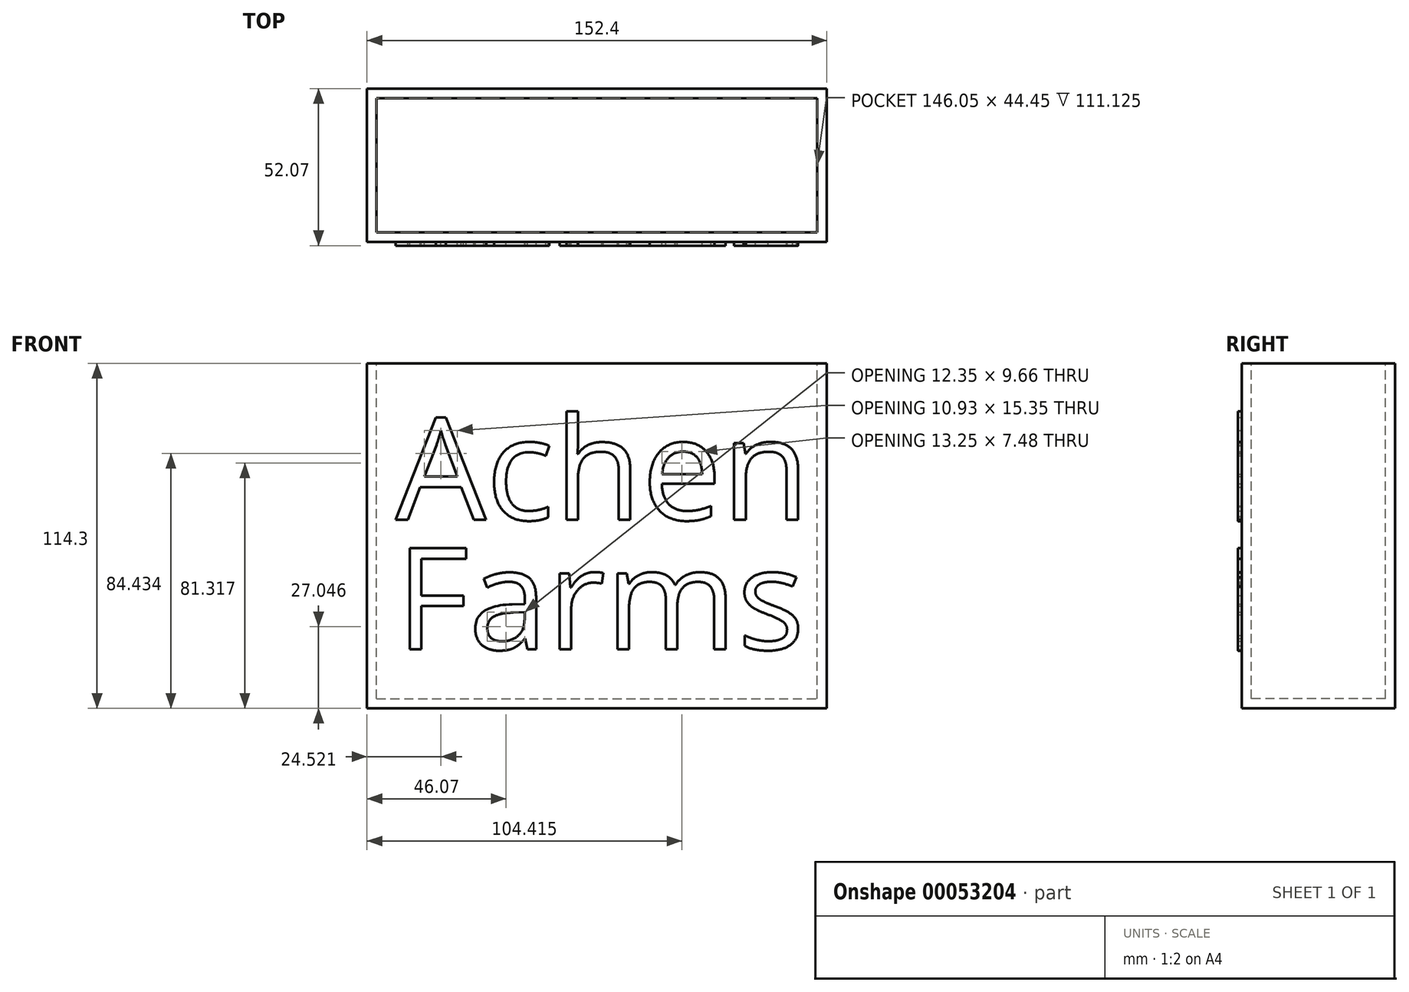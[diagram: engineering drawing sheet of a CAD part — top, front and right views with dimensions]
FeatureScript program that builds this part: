
annotation { "Feature Type Name" : "Feature", "Feature Type Description" : "" }
export const myFeature = defineFeature(function(context is Context, id is Id, definition is map)
    precondition{}
    {
        {
            var Q0;
            Q0=qCreatedBy(makeId("Top.planeOp"),FACE);
            var sketch = newSketch(context, id + "F0", { "sketchPlane" : qUnion([Q0])});
            skLineSegment(sketch, "E0.rect.bottom", {"start": v(-76.2, 25.4) * mm, "end": v(76.2, 25.4) * mm});
            skLineSegment(sketch, "E0.rect.top", {"start": v(-76.2, -25.4) * mm, "end": v(76.2, -25.4) * mm});
            skLineSegment(sketch, "E0.rect.left", {"start": v(-76.2, 25.4) * mm, "end": v(-76.2, -25.4) * mm});
            skLineSegment(sketch, "E0.rect.right", {"start": v(76.2, 25.4) * mm, "end": v(76.2, -25.4) * mm});
            skPoint(sketch, "E0.rect.middle", {"position": v(0, 0) * mm});
            skSolve(sketch);
        }
        {
            var Q0;
            Q0=makeQuery(id+"F0.imprint","IMPRINT",FACE,{"disambiguationData":[TD([[makeQuery(id+"F0.imprint","IMPRINT",EDGE,{"derivedFrom":sQuery(id+"F0.wireOp",EDGE,"E0.rect.bottom")}),-1.0]])]});
            extrude(context, id + "F1", {"entities" : qUnion([Q0]), "oppositeDirection" : true, "depth" : 114.3 * mm});
        }
        {
            var Q0;
            Q0=makeQuery(id+"F1.opExtrude","CAP_FACE",FACE,{"disambiguationData":[OSD([sQuery(id+"F0.wireOp",EDGE,"E0.rect.bottom"),sQuery(id+"F0.wireOp",EDGE,"E0.rect.top"),sQuery(id+"F0.wireOp",EDGE,"E0.rect.left"),sQuery(id+"F0.wireOp",EDGE,"E0.rect.right")])],"isStart":true});
            shell(context, id + "F2", {"entities" : qUnion([Q0]), "thickness" : 3.17 * mm});
        }
        {
            var Q0;
            Q0=makeQuery(id+"F1.opExtrude","SWEPT_FACE",FACE,{"disambiguationData":[OSD([sQuery(id+"F0.wireOp",EDGE,"E0.rect.top")])]});
            var sketch = newSketch(context, id + "F3", { "sketchPlane" : qUnion([Q0])});
            skText(sketch, "E1", { "text": "Achen", "fontName": "OpenSans-Regular.ttf"});
            skText(sketch, "E2", { "text": "Farms", "fontName": "OpenSans-Regular.ttf"});
            const initialGuessF3  = {"E1": [-0.06667, -0.05182, 1, 0, 0.03408], "E2": [-0.06667, -0.09477, 1, 0, 0.03379]};
            skSetInitialGuess(sketch, initialGuessF3);
            skSolve(sketch);
        }
        {
            var Q0;
            Q0 = qSketchRegion(id + "F3", true);
            extrude(context, id + "F4", {"entities" : qUnion([Q0]), "depth" : 1.27 * mm});
        }
    });
